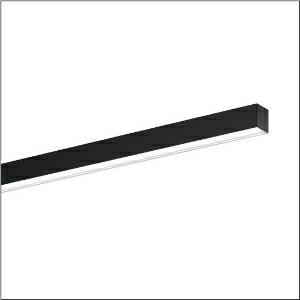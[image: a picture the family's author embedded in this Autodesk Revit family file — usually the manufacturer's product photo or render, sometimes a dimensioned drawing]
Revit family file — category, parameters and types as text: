
# Revit family: silica_r__21_51mx20tbt2b_b214
name_source: partatom
category: Lighting Fixtures
units: mm (PartAtom-declared; Revit-internal decimal feet)

## family parameters
Cut with Voids When Loaded = No
Host = Face
Light Source = No
Part Type = Normal
Room Calculation Point = No
Round Connector Dimension = Use Diameter
Shared = No

## types (1)
- --- (1 x LED, 3000 lm, 25.6 W, 6500K)
    Apparent Load = 26 VA
    CIE Flux Codes = 48 79 96 100 100
    Color Rendering = 80
    Color Temperature = 6500K
    Default Elevation = 1800 mm
    Description = Silica® 21, office luminaire, primary optical cover: cover, of PMMA, opal, light emission: direct distribution, primary light characteristic: symmetric, installation type: surface-mounted, LED, rated luminous flux: 3.000lm, luminous efficacy: 112lm/W, light colour: 8tw, colour temperature: 2700..6500K, control gear: DALI DT8, with terminal, 3+2-pole, max. 2.5mm², mains connection: 220..240V, AC, 50/60Hz, rated input power: 26.9W, luminaire housing, of aluminium, matt jet black (RAL 9005), length: 1.504mm, width: 53mm, height: 53mm, protection rating (complete): IP20, insulation class (complete): insulation class I (protective earthing), certification: CE, permissible operating ambient temperature: 0..+35°C, standard: EN 50419, packaging unit: 1 piece
    Height = 53 mm
    Lamp = 1 x LED
    Lamp Light Flux = 3000 lm
    Lamp Power = 25.6 W
    Lamp count = 1
    Length = 1504 mm
    Luminous efficacy = 117 lm/W
    Manufacturer = Siteco
    ModVariant = No
    Model = 51MX20TBT2B
    Mounting Place = Ceiling
    Mounting Type = Surface mounted
    Number of Poles = 1
    OnlyDefault = Yes
    Power Factor = 1
    Product Name = Silica® 21
    Product group = office luminaire | ceiling mounted
    ProductGroupID = 303
    Protection Class = Protection class I
    Protection Degree = IP 20
    RLX_Detail_Level = 1
    RLX_Emergency_Light_Flux = 0 lm
    RLX_Emergency_Type = 0
    RLX_Emergency_Type_DB = No
    RlxData = <blob elided: 25589 chars, md5=0c4b98a8>
    Socket = socket
    Standby Power = 0 W
    System Light Flux = 3000 lm
    System Power = 26 W
    Type Comments = individual setting
    Type Image = l_1335925.jpg
    URL = http://relux.com
    VarID = @adj_161165
    Voltage = 0 V
    Weight = 0.00 kg
    Width = 53 mm

## geometry (parser evidence)
native form markers: Blend x4, Sweep x9
no freeform markers — native parametric forms only
